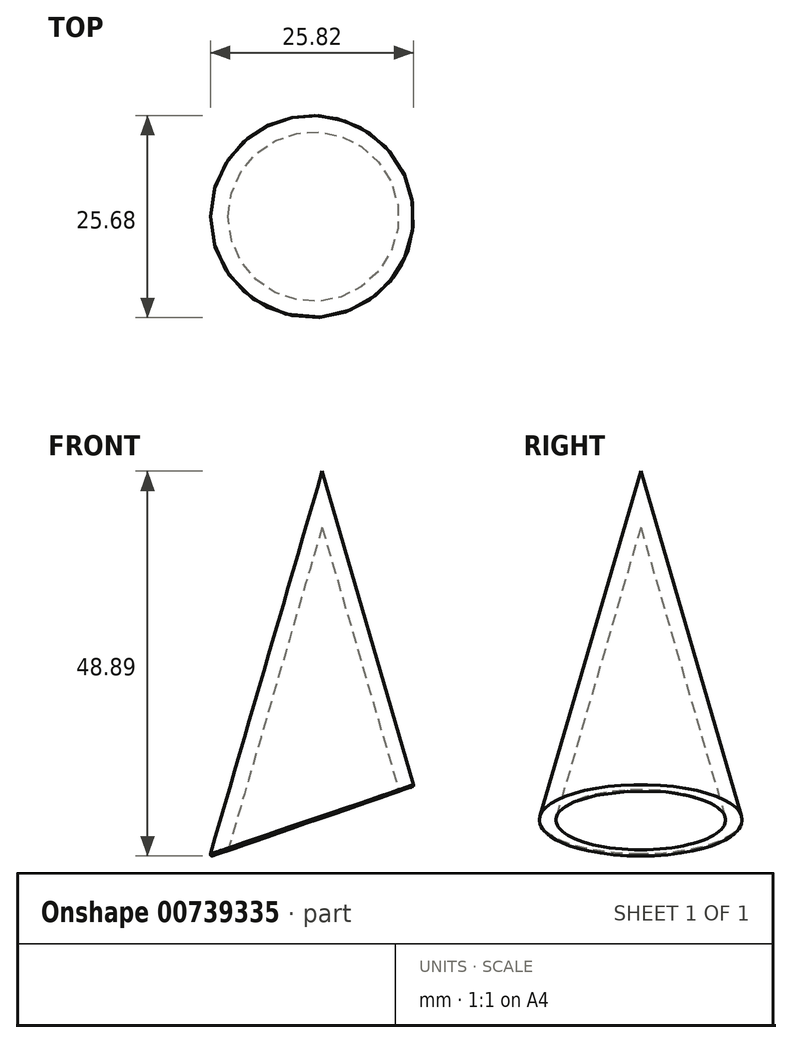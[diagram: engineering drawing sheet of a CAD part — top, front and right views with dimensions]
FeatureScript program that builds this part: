
annotation { "Feature Type Name" : "Feature", "Feature Type Description" : "" }
export const myFeature = defineFeature(function(context is Context, id is Id, definition is map)
    precondition{}
    {
        {
            var Q0;
            Q0=qCreatedBy(makeId("Front.planeOp"),FACE);
            var sketch = newSketch(context, id + "F0", { "sketchPlane" : qUnion([Q0])});
            skLineSegment(sketch, "E0", {"start": v(0, -27.05) * mm, "end": v(17.5, -27.05) * mm});
            skLineSegment(sketch, "E1", {"start": v(17.5, -27.05) * mm, "end": v(0, 32.95) * mm});
            skLineSegment(sketch, "E2", {"start": v(0, 32.95) * mm, "end": v(0, -27.05) * mm});
            skLineSegment(sketch, "E3", {"start": v(0, 38.42) * mm, "end": v(-0.1, -43.64) * mm});
            skSolve(sketch);
        }
        {
            var Q0;
            Q0=makeQuery(id+"F0.imprint","IMPRINT",FACE,{"disambiguationData":[TD([[makeQuery(id+"F0.imprint","IMPRINT",EDGE,{"derivedFrom":sQuery(id+"F0.wireOp",EDGE,"E0")}),1.0]])]});
            var Q1;
            Q1=sQuery(id+"F0.wireOp",EDGE,"E2");
            revolve(context, id + "F1", {"surfaceOperationType" : NewSurfaceOperationType.NEW, "entities" : qUnion([Q0]), "axis" : qUnion([Q1]), "revolveType" : RevolveType.FULL});
        }
        {
            var Q0;
            Q0=makeQuery(id+"F1.opRevolve","SWEPT_EDGE",EDGE,{"disambiguationData":[OSD([sQuery(id+"F0.wireOp",EDGE,"E0"),sQuery(id+"F0.wireOp",EDGE,"E1")])]});
            fillet(context, id + "F2", {"entities" : qUnion([Q0]), "radius" : 1.5 * mm, "tangentPropagation" : true, "allowEdgeOverflow" : false});
        }
        {
            var Q0;
            Q0=qCreatedBy(makeId("Front.planeOp"),FACE);
            cPlane(context, id + "F3", {"entities" : qUnion([Q0]), "cplaneType" : CPlaneType.OFFSET, "offset" : 25 * mm, "width" : 150 * mm, "height" : 150 * mm});
        }
        {
            var Q0;
            Q0=qCreatedBy(id+"F3.planeOp",FACE);
            var sketch = newSketch(context, id + "F4", { "sketchPlane" : qUnion([Q0])});
            skLineSegment(sketch, "E4", {"start": v(-14.46, -16.12) * mm, "end": v(11.74, -7.04) * mm});
            skLineSegment(sketch, "E5", {"start": v(11.74, -7.04) * mm, "end": v(20.6, -7.15) * mm});
            skLineSegment(sketch, "E6", {"start": v(20.73, 38.03) * mm, "end": v(-22.23, 38.53) * mm});
            skLineSegment(sketch, "E7", {"start": v(-22.23, -16.07) * mm, "end": v(-14.46, -16.12) * mm});
            skLineSegment(sketch, "E8", {"start": v(-22.23, -16.07) * mm, "end": v(-22.23, -30.66) * mm});
            skLineSegment(sketch, "E9", {"start": v(-22.23, -30.66) * mm, "end": v(20.6, -30.66) * mm});
            skLineSegment(sketch, "E10", {"start": v(20.6, -30.66) * mm, "end": v(20.6, -7.15) * mm});
            skSolve(sketch);
        }
        {
            var Q0;
            Q0 = qSketchRegion(id + "F4", true);
            extrude(context, id + "F5", {"entities" : qUnion([Q0]), "operationType" : NewBodyOperationType.REMOVE, "oppositeDirection" : true, "depth" : 55.3 * mm, "offsetDistance" : 25 * mm});
        }
        {
            var Q0;
            Q0=makeQuery(id+"F5.boolean.opBoolean","COPY",FACE,{"derivedFrom":makeQuery(id+"F5.opExtrude","SWEPT_FACE",FACE,{"disambiguationData":[OSD([sQuery(id+"F4.wireOp",EDGE,"E4")])]})});
            shell(context, id + "F6", {"entities" : qUnion([Q0]), "thickness" : 2 * mm});
        }
        {
            var Q0;
            Q0=makeQuery(id+"F5.boolean.opBoolean","INTERSECT",EDGE,{"derivedFrom":[makeQuery(id+"F1.opRevolve","SWEPT_FACE",FACE,{"disambiguationData":[OSD([sQuery(id+"F0.wireOp",EDGE,"E1")])]}),makeQuery(id+"F5.opExtrude","SWEPT_FACE",FACE,{"disambiguationData":[OSD([sQuery(id+"F4.wireOp",EDGE,"E4")])]})]});
            fillet(context, id + "F7", {"entities" : qUnion([Q0]), "radius" : .2 * mm, "tangentPropagation" : true, "allowEdgeOverflow" : false});
        }
        {
            var Q0;
            Q0=makeQuery(id+"F6.opShell","OFFSET_EDGE",EDGE,{"disambiguationData":[OSD([sQuery(id+"F0.wireOp",EDGE,"E1"),sQuery(id+"F4.wireOp",EDGE,"E4")])]});
            fillet(context, id + "F8", {"entities" : qUnion([Q0]), "radius" : .2 * mm, "tangentPropagation" : true, "allowEdgeOverflow" : false});
        }
    });
